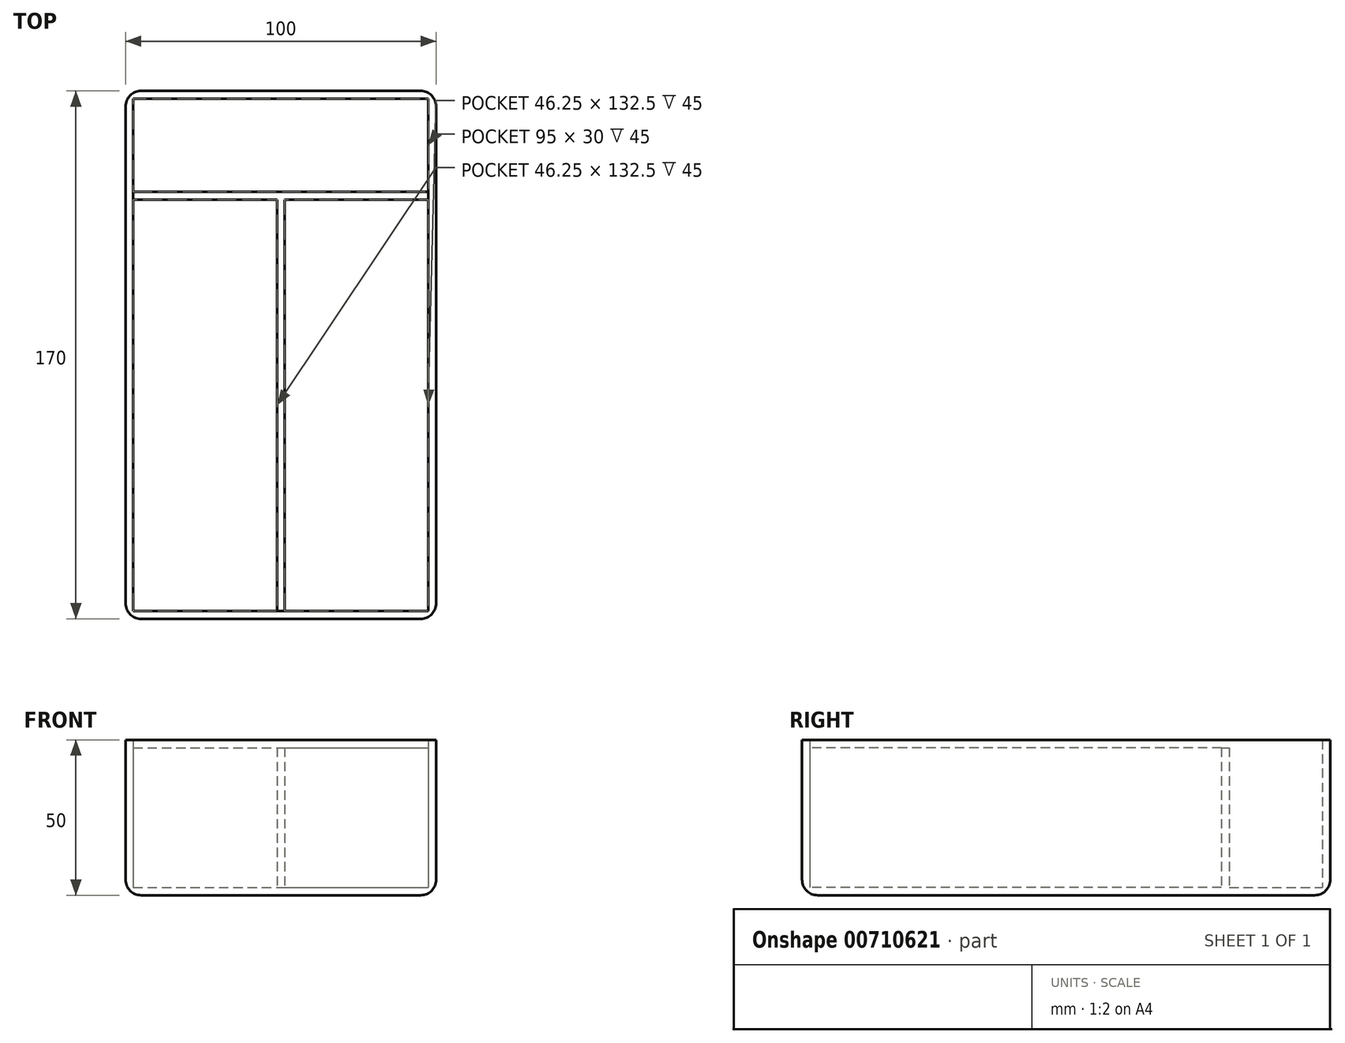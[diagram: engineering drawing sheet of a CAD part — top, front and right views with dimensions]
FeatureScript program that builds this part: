
annotation { "Feature Type Name" : "Feature", "Feature Type Description" : "" }
export const myFeature = defineFeature(function(context is Context, id is Id, definition is map)
    precondition{}
    {
        {
            var Q0;
            Q0=qCreatedBy(makeId("Top.planeOp"),FACE);
            var sketch = newSketch(context, id + "F0", { "sketchPlane" : qUnion([Q0])});
            skLineSegment(sketch, "E0.bottom", {"start": v(0, 0) * mm, "end": v(100, 0) * mm});
            skLineSegment(sketch, "E0.top", {"start": v(0, 170) * mm, "end": v(100, 170) * mm});
            skLineSegment(sketch, "E0.left", {"start": v(0, 0) * mm, "end": v(0, 170) * mm});
            skLineSegment(sketch, "E0.right", {"start": v(100, 0) * mm, "end": v(100, 170) * mm});
            skSolve(sketch);
        }
        {
            var Q0;
            Q0=makeQuery(id+"F0.imprint","IMPRINT",FACE,{"disambiguationData":[TD([[makeQuery(id+"F0.imprint","IMPRINT",EDGE,{"derivedFrom":sQuery(id+"F0.wireOp",EDGE,"E0.bottom")}),1.0]])]});
            extrude(context, id + "F1", {"entities" : qUnion([Q0]), "depth" : 50 * mm, "offsetDistance" : 25 * mm});
        }
        {
            var Q0;
            Q0=makeQuery(id+"F1.opExtrude","CAP_FACE",FACE,{"disambiguationData":[OSD([sQuery(id+"F0.wireOp",EDGE,"E0.bottom"),sQuery(id+"F0.wireOp",EDGE,"E0.top"),sQuery(id+"F0.wireOp",EDGE,"E0.left"),sQuery(id+"F0.wireOp",EDGE,"E0.right")])],"isStart":false});
            shell(context, id + "F2", {"entities" : qUnion([Q0]), "thickness" : 2.5 * mm});
        }
        {
            var Q0;
            Q0=makeQuery(id+"F1.opExtrude","SWEPT_EDGE",EDGE,{"disambiguationData":[OSD([sQuery(id+"F0.wireOp",EDGE,"E0.top"),sQuery(id+"F0.wireOp",EDGE,"E0.right")])]});
            var Q1;
            Q1=makeQuery(id+"F1.opExtrude","CAP_EDGE",EDGE,{"disambiguationData":[OSD([sQuery(id+"F0.wireOp",EDGE,"E0.right")])],"isStart":true});
            var Q2;
            Q2=makeQuery(id+"F1.opExtrude","SWEPT_EDGE",EDGE,{"disambiguationData":[OSD([sQuery(id+"F0.wireOp",EDGE,"E0.bottom"),sQuery(id+"F0.wireOp",EDGE,"E0.right")])]});
            var Q3;
            Q3=makeQuery(id+"F1.opExtrude","SWEPT_EDGE",EDGE,{"disambiguationData":[OSD([sQuery(id+"F0.wireOp",EDGE,"E0.bottom"),sQuery(id+"F0.wireOp",EDGE,"E0.left")])]});
            var Q4;
            Q4=makeQuery(id+"F1.opExtrude","CAP_EDGE",EDGE,{"disambiguationData":[OSD([sQuery(id+"F0.wireOp",EDGE,"E0.bottom")])],"isStart":true});
            var Q5;
            Q5=makeQuery(id+"F1.opExtrude","CAP_EDGE",EDGE,{"disambiguationData":[OSD([sQuery(id+"F0.wireOp",EDGE,"E0.left")])],"isStart":true});
            var Q6;
            Q6=makeQuery(id+"F1.opExtrude","CAP_EDGE",EDGE,{"disambiguationData":[OSD([sQuery(id+"F0.wireOp",EDGE,"E0.top")])],"isStart":true});
            var Q7;
            Q7=makeQuery(id+"F1.opExtrude","SWEPT_EDGE",EDGE,{"disambiguationData":[OSD([sQuery(id+"F0.wireOp",EDGE,"E0.top"),sQuery(id+"F0.wireOp",EDGE,"E0.left")])]});
            fillet(context, id + "F3", {"entities" : qUnion([Q0, Q1, Q2, Q3, Q4, Q5, Q6, Q7]), "radius" : 5 * mm, "tangentPropagation" : true, "allowEdgeOverflow" : false});
        }
        {
            var Q0;
            Q0=makeQuery(id+"F2.opShell","OFFSET_FACE",FACE,{"disambiguationData":[OSD([sQuery(id+"F0.wireOp",EDGE,"E0.bottom"),sQuery(id+"F0.wireOp",EDGE,"E0.top"),sQuery(id+"F0.wireOp",EDGE,"E0.left"),sQuery(id+"F0.wireOp",EDGE,"E0.right")])]});
            var sketch = newSketch(context, id + "F4", { "sketchPlane" : qUnion([Q0])});
            skLineSegment(sketch, "E1.bottom", {"start": v(2.5, 135) * mm, "end": v(97.5, 135) * mm});
            skLineSegment(sketch, "E1.top", {"start": v(2.5, 137.5) * mm, "end": v(97.5, 137.5) * mm});
            skLineSegment(sketch, "E1.left", {"start": v(2.5, 135) * mm, "end": v(2.5, 137.5) * mm});
            skLineSegment(sketch, "E1.right", {"start": v(97.5, 135) * mm, "end": v(97.5, 137.5) * mm});
            skSolve(sketch);
        }
        {
            var Q0;
            Q0 = qSketchRegion(id + "F4", true);
            extrude(context, id + "F5", {"entities" : qUnion([Q0]), "operationType" : NewBodyOperationType.ADD, "depth" : 45 * mm, "offsetDistance" : 25 * mm});
        }
        {
            var Q0;
            {var subQ0=sQuery(id+"F0.wireOp",EDGE,"E0.bottom");var subQ1=sQuery(id+"F0.wireOp",EDGE,"E0.left");var subQ2=sQuery(id+"F0.wireOp",EDGE,"E0.right");Q0=makeQuery(id+"F5.boolean.opBoolean","SPLIT",FACE,{"disambiguationData":[TD([makeQuery(id+"F2.opShell","OFFSET_FACE",FACE,{"disambiguationData":[OSD([subQ0])]})])],"derivedFrom":makeQuery(id+"F2.opShell","OFFSET_FACE",FACE,{"disambiguationData":[OSD([subQ0,sQuery(id+"F0.wireOp",EDGE,"E0.top"),subQ1,subQ2])]})});}
            var sketch = newSketch(context, id + "F6", { "sketchPlane" : qUnion([Q0])});
            skLineSegment(sketch, "E2.bottom", {"start": v(51.25, 135) * mm, "end": v(48.75, 135) * mm});
            skLineSegment(sketch, "E2.top", {"start": v(51.25, 2.5) * mm, "end": v(48.75, 2.5) * mm});
            skLineSegment(sketch, "E2.left", {"start": v(51.25, 135) * mm, "end": v(51.25, 2.5) * mm});
            skLineSegment(sketch, "E2.right", {"start": v(48.75, 135) * mm, "end": v(48.75, 2.5) * mm});
            skSolve(sketch);
        }
        {
            var Q0;
            Q0=makeQuery(id+"F6.imprint","IMPRINT",FACE,{"disambiguationData":[TD([[makeQuery(id+"F6.imprint","IMPRINT",EDGE,{"derivedFrom":sQuery(id+"F6.wireOp",EDGE,"E2.bottom")}),-1.0]])]});
            extrude(context, id + "F7", {"entities" : qUnion([Q0]), "operationType" : NewBodyOperationType.ADD, "depth" : 45 * mm, "offsetDistance" : 25 * mm});
        }
    });
